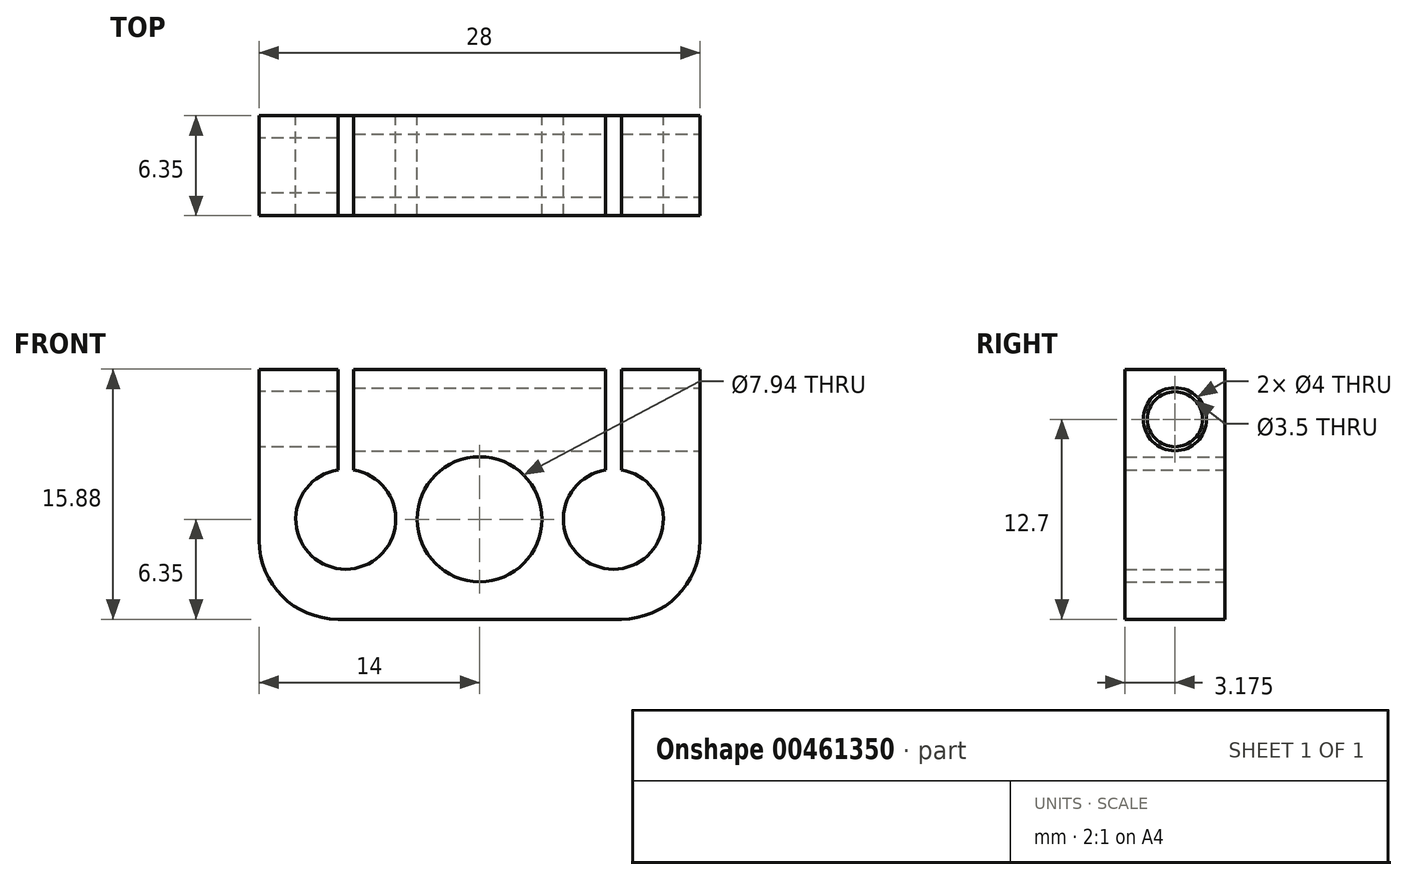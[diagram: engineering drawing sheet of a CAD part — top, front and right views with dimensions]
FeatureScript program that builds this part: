
annotation { "Feature Type Name" : "Feature", "Feature Type Description" : "" }
export const myFeature = defineFeature(function(context is Context, id is Id, definition is map)
    precondition{}
    {
        {
            var Q0;
            Q0=qCreatedBy(makeId("Front.planeOp"),FACE);
            var sketch = newSketch(context, id + "F0", { "sketchPlane" : qUnion([Q0])});
            skCircle(sketch, "E0", {"center": v(0, 0) * mm, "radius": 3.97 * mm});
            skCircle(sketch, "E1", {"center": v(8.5, 0) * mm, "radius": 3.18 * mm});
            skLineSegment(sketch, "E2", {"start": v(0, 22.35) * mm, "end": v(0, -31.33) * mm});
            skCircle(sketch, "E3.MirrorC", {"center": v(-8.5, 0) * mm, "radius": 3.18 * mm});
            skLineSegment(sketch, "E4.bottom", {"start": v(-14, -6.35) * mm, "end": v(14, -6.35) * mm});
            skLineSegment(sketch, "E4.top", {"start": v(-14, 9.53) * mm, "end": v(14, 9.53) * mm});
            skLineSegment(sketch, "E4.left", {"start": v(-14, -6.35) * mm, "end": v(-14, 9.53) * mm});
            skLineSegment(sketch, "E4.right", {"start": v(14, -6.35) * mm, "end": v(14, 9.53) * mm});
            skLineSegment(sketch, "E5.bottom", {"start": v(9, 11) * mm, "end": v(8, 11) * mm});
            skLineSegment(sketch, "E5.top", {"start": v(9, 2) * mm, "end": v(8, 2) * mm});
            skLineSegment(sketch, "E5.left", {"start": v(9, 11) * mm, "end": v(9, 2) * mm});
            skLineSegment(sketch, "E5.right", {"start": v(8, 11) * mm, "end": v(8, 2) * mm});
            skPoint(sketch, "E5.middle", {"position": v(8.5, 6.5) * mm});
            skLineSegment(sketch, "E6.MirrorCS", {"start": v(-8, 11) * mm, "end": v(-8, 2) * mm});
            skLineSegment(sketch, "E7.MirrorCS", {"start": v(-9, 11) * mm, "end": v(-9, 2) * mm});
            skLineSegment(sketch, "E8.MirrorCS", {"start": v(-9, 2) * mm, "end": v(-8, 2) * mm});
            skLineSegment(sketch, "E9.MirrorCS", {"start": v(-9, 11) * mm, "end": v(-8, 11) * mm});
            skPoint(sketch, "E10.MirrorP", {"position": v(-8.5, 6.5) * mm});
            skSolve(sketch);
        }
        {
            var Q0;
            {var subQ10=sQuery(id+"F0.wireOp",EDGE,"E4.left");Q0=makeQuery(id+"F0.imprint","IMPRINT",FACE,{"disambiguationData":[TD([[makeQuery(id+"F0.imprint","IMPRINT",EDGE,{"derivedFrom":subQ10}),-1.0]])]});}
            var Q1;
            {var subQ14=sQuery(id+"F0.wireOp",EDGE,"E4.right");Q1=makeQuery(id+"F0.imprint","IMPRINT",FACE,{"disambiguationData":[TD([[makeQuery(id+"F0.imprint","IMPRINT",EDGE,{"derivedFrom":subQ14}),1.0]])]});}
            extrude(context, id + "F1", {"entities" : qUnion([Q0, Q1]), "depth" : 6.35 * mm});
        }
        {
            var Q0;
            Q0=makeQuery(id+"F1.opExtrude","SWEPT_FACE",FACE,{"disambiguationData":[OSD([sQuery(id+"F0.wireOp",EDGE,"E4.right")])]});
            var sketch = newSketch(context, id + "F2", { "sketchPlane" : qUnion([Q0])});
            skCircle(sketch, "E11", {"center": v(-3.18, 6.35) * mm, "radius": 2 * mm});
            skSolve(sketch);
        }
        {
            var Q0;
            Q0=makeQuery(id+"F2.imprint","IMPRINT",FACE,{"disambiguationData":[TD([[makeQuery(id+"F2.imprint","IMPRINT",EDGE,{"derivedFrom":sQuery(id+"F2.wireOp",EDGE,"E11")}),1.0]])]});
            var Q1;
            Q1=makeQuery(id+"F2.imprint","IMPRINT",FACE,{"disambiguationData":[TD([[makeQuery(id+"F2.imprint","IMPRINT",EDGE,{"derivedFrom":sQuery(id+"F2.wireOp",EDGE,"dMZyHBpA-FFhW-6PNP-TJlC-QGw5MgTyNsU1")}),1.0]])]});
            extrude(context, id + "F3", {"entities" : qUnion([Q0, Q1]), "operationType" : NewBodyOperationType.REMOVE, "oppositeDirection" : true, "depth" : 22.5 * mm});
        }
        {
            var Q0;
            Q0=makeQuery(id+"F1.opExtrude","SWEPT_EDGE",EDGE,{"disambiguationData":[OSD([sQuery(id+"F0.wireOp",EDGE,"E4.bottom"),sQuery(id+"F0.wireOp",EDGE,"E4.right")])]});
            var Q1;
            Q1=makeQuery(id+"F1.opExtrude","SWEPT_EDGE",EDGE,{"disambiguationData":[OSD([sQuery(id+"F0.wireOp",EDGE,"E4.bottom"),sQuery(id+"F0.wireOp",EDGE,"E4.left")])]});
            fillet(context, id + "F4", {"entities" : qUnion([Q0, Q1]), "radius" : 5 * mm, "tangentPropagation" : true, "allowEdgeOverflow" : false});
        }
        {
            var Q0;
            Q0=makeQuery(id+"F1.opExtrude","SWEPT_FACE",FACE,{"disambiguationData":[OSD([sQuery(id+"F0.wireOp",EDGE,"E4.left")])]});
            var sketch = newSketch(context, id + "F5", { "sketchPlane" : qUnion([Q0])});
            skCircle(sketch, "E12", {"center": v(3.17, 6.35) * mm, "radius": 1.75 * mm});
            skSolve(sketch);
        }
        {
            var Q0;
            Q0=makeQuery(id+"F5.imprint","IMPRINT",FACE,{"disambiguationData":[TD([[makeQuery(id+"F5.imprint","IMPRINT",EDGE,{"derivedFrom":sQuery(id+"F5.wireOp",EDGE,"E12")}),1.0]])]});
            extrude(context, id + "F6", {"entities" : qUnion([Q0]), "operationType" : NewBodyOperationType.REMOVE, "endBound" : BoundingType.THROUGH_ALL, "oppositeDirection" : true, "depth" : 25 * mm});
        }
    });
